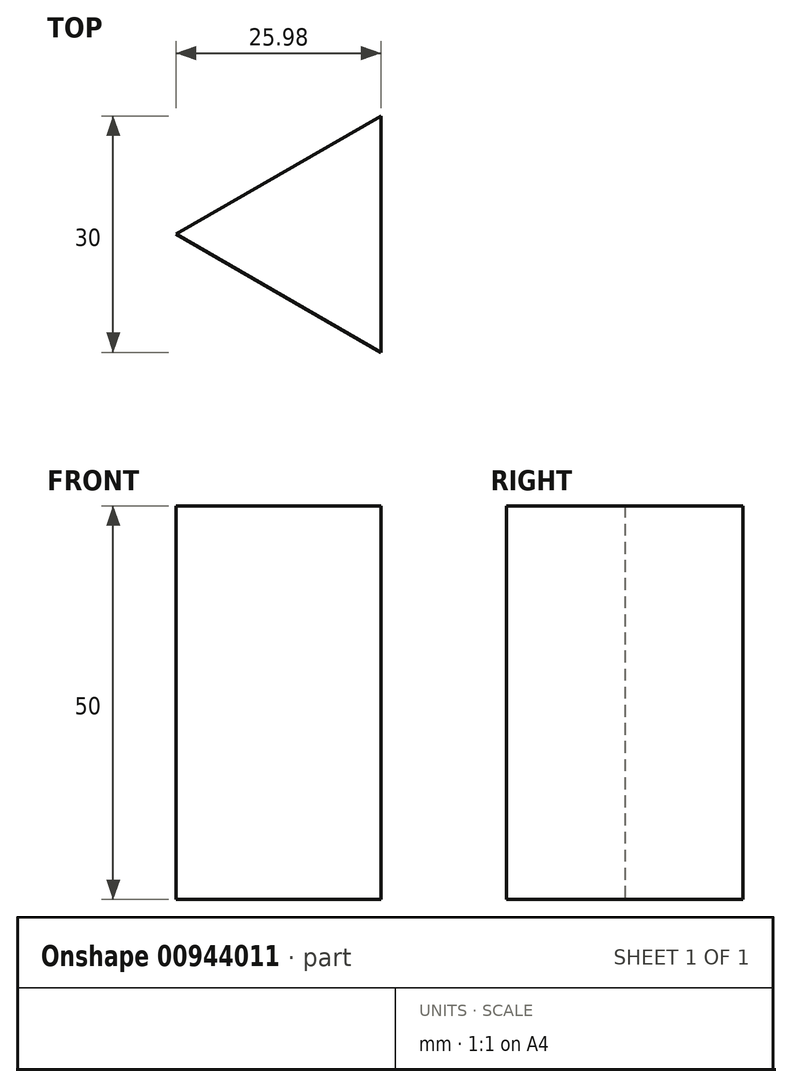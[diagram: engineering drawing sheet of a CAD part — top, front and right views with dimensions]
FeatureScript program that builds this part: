
annotation { "Feature Type Name" : "Feature", "Feature Type Description" : "" }
export const myFeature = defineFeature(function(context is Context, id is Id, definition is map)
    precondition{}
    {
        {
            var Q0;
            Q0=qCreatedBy(makeId("Top.planeOp"),FACE);
            var sketch = newSketch(context, id + "F0", { "sketchPlane" : qUnion([Q0])});
            skCircle(sketch, "E0.cCircle", {"center": v(0, 0) * mm, "radius": 8.66 * mm, "construction": true});
            skLineSegment(sketch, "E0.0", {"start": v(8.66, -15) * mm, "end": v(8.66, 15) * mm});
            skLineSegment(sketch, "E0.1", {"start": v(-17.32, 0) * mm, "end": v(8.66, -15) * mm});
            skLineSegment(sketch, "E0.2", {"start": v(8.66, 15) * mm, "end": v(-17.32, 0) * mm});
            skPoint(sketch, "E0.0.midPoint", {"position": v(8.66, 0) * mm});
            skSolve(sketch);
        }
        {
            var Q0;
            Q0 = qSketchRegion(id + "F0", true);
            extrude(context, id + "F1", {"entities" : qUnion([Q0]), "depth" : 50 * mm, "offsetDistance" : 25 * mm});
        }
    });
